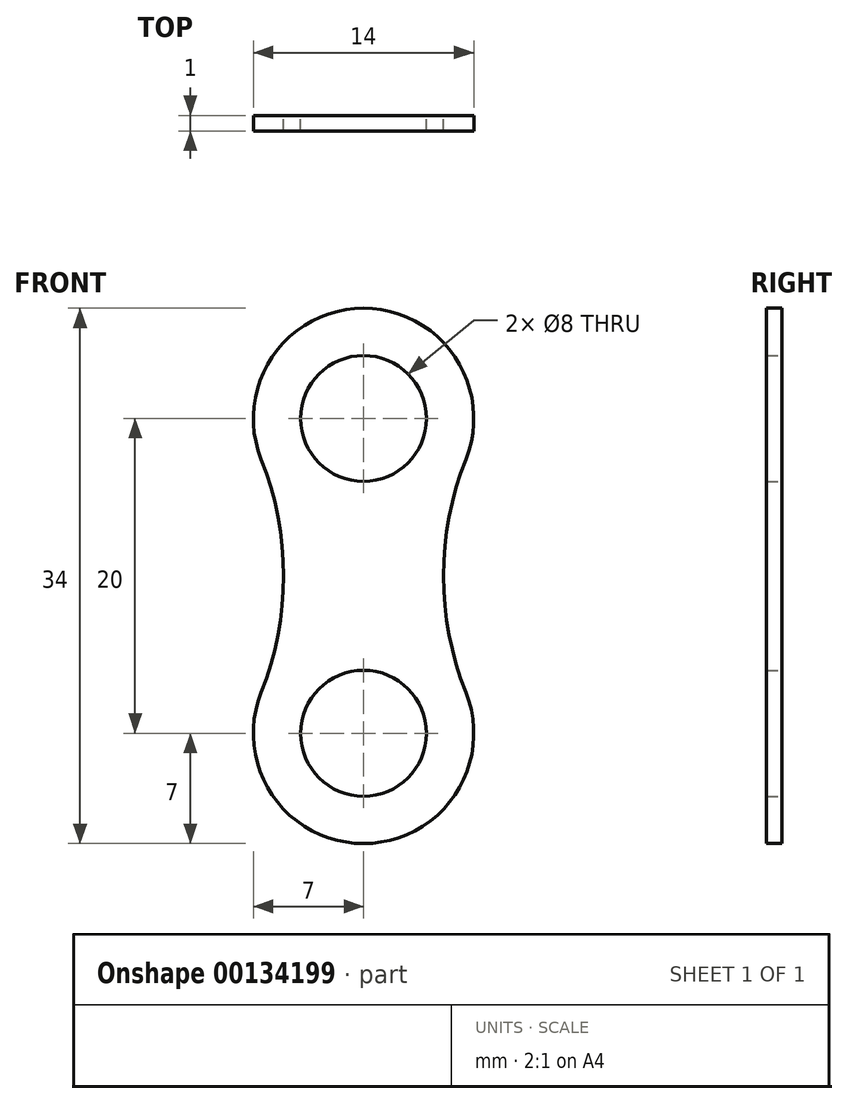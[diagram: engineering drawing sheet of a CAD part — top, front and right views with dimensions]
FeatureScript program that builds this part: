
annotation { "Feature Type Name" : "Feature", "Feature Type Description" : "" }
export const myFeature = defineFeature(function(context is Context, id is Id, definition is map)
    precondition{}
    {
        {
            var Q0;
            Q0=qCreatedBy(makeId("Front.planeOp"),FACE);
            var sketch = newSketch(context, id + "F0", { "sketchPlane" : qUnion([Q0])});
            skArc(sketch, "E0", {"start": v(6.5, -2.6) * mm, "mid": v(0, 7) * mm, "end": v(-6.5, -2.6) * mm});
            skCircle(sketch, "E1", {"center": v(0, 0) * mm, "radius": 4 * mm});
            skCircle(sketch, "E2", {"center": v(0, -20) * mm, "radius": 4 * mm});
            skArc(sketch, "E3", {"start": v(-6.5, -17.4) * mm, "mid": v(0, -27) * mm, "end": v(6.5, -17.4) * mm});
            skArc(sketch, "E4", {"start": v(-6.5, -17.4) * mm, "mid": v(-5.08, -10) * mm, "end": v(-6.5, -2.6) * mm});
            skArc(sketch, "E5", {"start": v(6.5, -2.6) * mm, "mid": v(5.08, -10) * mm, "end": v(6.5, -17.4) * mm});
            skSolve(sketch);
        }
        {
            var Q0;
            Q0=makeQuery(id+"F0.imprint","IMPRINT",FACE,{"disambiguationData":[TD([[makeQuery(id+"F0.imprint","IMPRINT",EDGE,{"derivedFrom":sQuery(id+"F0.wireOp",EDGE,"E0")}),1.0]])]});
            extrude(context, id + "F1", {"entities" : qUnion([Q0]), "depth" : 1 * mm});
        }
    });
